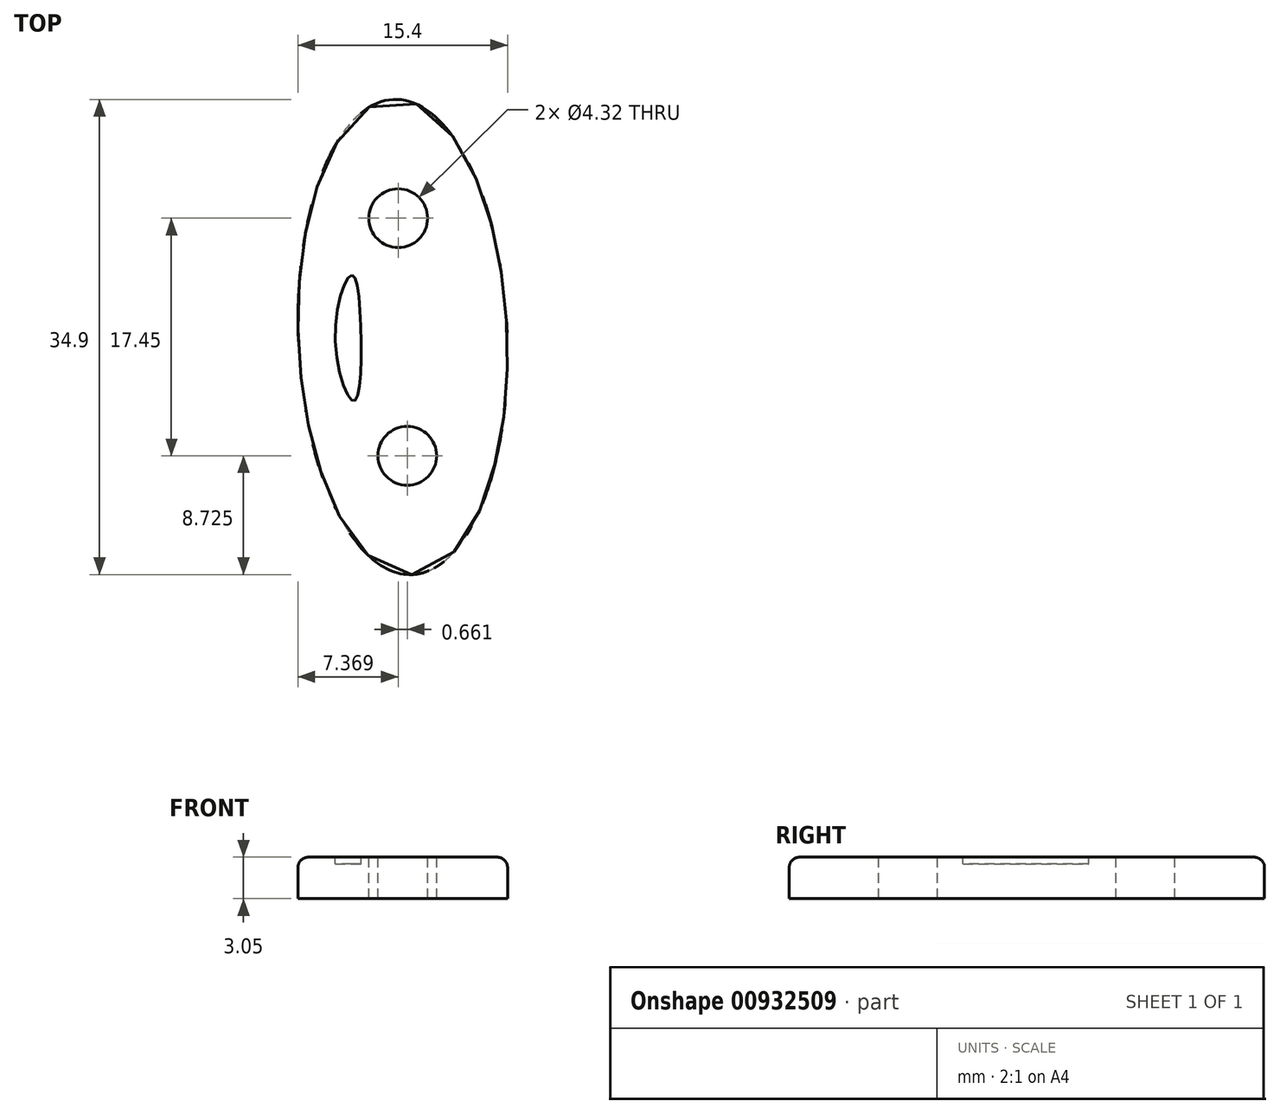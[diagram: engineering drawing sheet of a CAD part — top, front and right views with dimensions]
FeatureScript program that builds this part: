
annotation { "Feature Type Name" : "Feature", "Feature Type Description" : "" }
export const myFeature = defineFeature(function(context is Context, id is Id, definition is map)
    precondition{}
    {
        {
            var Q0;
            Q0=qCreatedBy(makeId("Top.planeOp"),FACE);
            var sketch = newSketch(context, id + "F0", { "sketchPlane" : qUnion([Q0])});
            skEllipse(sketch, "E0", {"center": v(0, 0) * mm, "majorRadius": 17.46 * mm, "minorRadius": 7.67 * mm, "majorAxis": v(0.04, -1)});
            skSolve(sketch);
        }
        {
            var Q0;
            Q0 = qSketchRegion(id + "F0", true);
            extrude(context, id + "F1", {"entities" : qUnion([Q0]), "depth" : 3.05 * mm, "offsetDistance" : 25.4 * mm});
        }
        {
            var Q0;
            Q0=makeQuery(id+"F1.opExtrude","CAP_FACE",FACE,{"disambiguationData":[OSD([sQuery(id+"F0.wireOp",EDGE,"E0")])],"isStart":false});
            var sketch = newSketch(context, id + "F2", { "sketchPlane" : qUnion([Q0])});
            skPoint(sketch, "E1.0.internal.snap0", {"position": v(-0.66, 17.45) * mm});
            skCircle(sketch, "E2", {"center": v(0.33, -8.72) * mm, "radius": 2.16 * mm});
            skSolve(sketch);
        }
        {
            var Q0;
            Q0 = qSketchRegion(id + "F2", true);
            extrude(context, id + "F3", {"entities" : qUnion([Q0]), "operationType" : NewBodyOperationType.REMOVE, "oppositeDirection" : true, "depth" : 25.4 * mm, "offsetDistance" : 25.4 * mm});
        }
        {
            var Q0;
            Q0=makeQuery(id+"F1.opExtrude","CAP_FACE",FACE,{"disambiguationData":[OSD([sQuery(id+"F0.wireOp",EDGE,"E0")])],"isStart":false});
            var sketch = newSketch(context, id + "F4", { "sketchPlane" : qUnion([Q0])});
            skLineSegment(sketch, "E3", {"start": v(-0.66, 17.45) * mm, "end": v(0.66, -17.45) * mm});
            skLineSegment(sketch, "E4", {"start": v(0, 0) * mm, "end": v(-0.66, 17.45) * mm});
            skLineSegment(sketch, "E5", {"start": v(0, 0) * mm, "end": v(-0.33, 8.72) * mm});
            skCircle(sketch, "E6", {"center": v(-0.33, 8.72) * mm, "radius": 2.16 * mm});
            skSolve(sketch);
        }
        {
            var Q0;
            Q0 = qSketchRegion(id + "F4", true);
            extrude(context, id + "F5", {"entities" : qUnion([Q0]), "operationType" : NewBodyOperationType.REMOVE, "oppositeDirection" : true, "depth" : 25.4 * mm, "offsetDistance" : 25.4 * mm});
        }
        {
            var Q0;
            Q0=makeQuery(id+"F3.boolean.opBoolean","COPY",EDGE,{"derivedFrom":makeQuery(id+"F3.opExtrude","CAP_EDGE",EDGE,{"disambiguationData":[OSD([sQuery(id+"F2.wireOp",EDGE,"E2")])],"isStart":true})});
            var Q1;
            Q1=makeQuery(id+"F1.opExtrude","CAP_EDGE",EDGE,{"disambiguationData":[OSD([sQuery(id+"F0.wireOp",EDGE,"E0")])],"isStart":false});
            var Q2;
            Q2=makeQuery(id+"F5.boolean.opBoolean","COPY",EDGE,{"derivedFrom":makeQuery(id+"F5.opExtrude","CAP_EDGE",EDGE,{"disambiguationData":[OSD([sQuery(id+"F4.wireOp",EDGE,"E6")])],"isStart":true})});
            fillet(context, id + "F6", {"entities" : qUnion([Q0, Q1, Q2]), "radius" : 0.76 * mm, "tangentPropagation" : true, "allowEdgeOverflow" : false});
        }
        {
            var Q0;
            Q0=makeQuery(id+"F1.opExtrude","CAP_FACE",FACE,{"disambiguationData":[OSD([sQuery(id+"F0.wireOp",EDGE,"E0")])],"isStart":false});
            var sketch = newSketch(context, id + "F7", { "sketchPlane" : qUnion([Q0])});
            skFitSpline(sketch, "E7", {"points": [v(-3.73, 4.54) * mm, v(-4.97, 0) * mm, v(-3.6, -4.7) * mm, v(-3.07, 0) * mm, v(-3.73, 4.54) * mm]});
            skSolve(sketch);
        }
        {
            var Q0;
            Q0 = qSketchRegion(id + "F7", true);
            extrude(context, id + "F8", {"entities" : qUnion([Q0]), "operationType" : NewBodyOperationType.REMOVE, "oppositeDirection" : true, "depth" : 0.5 * mm, "offsetDistance" : 25.4 * mm});
        }
    });
